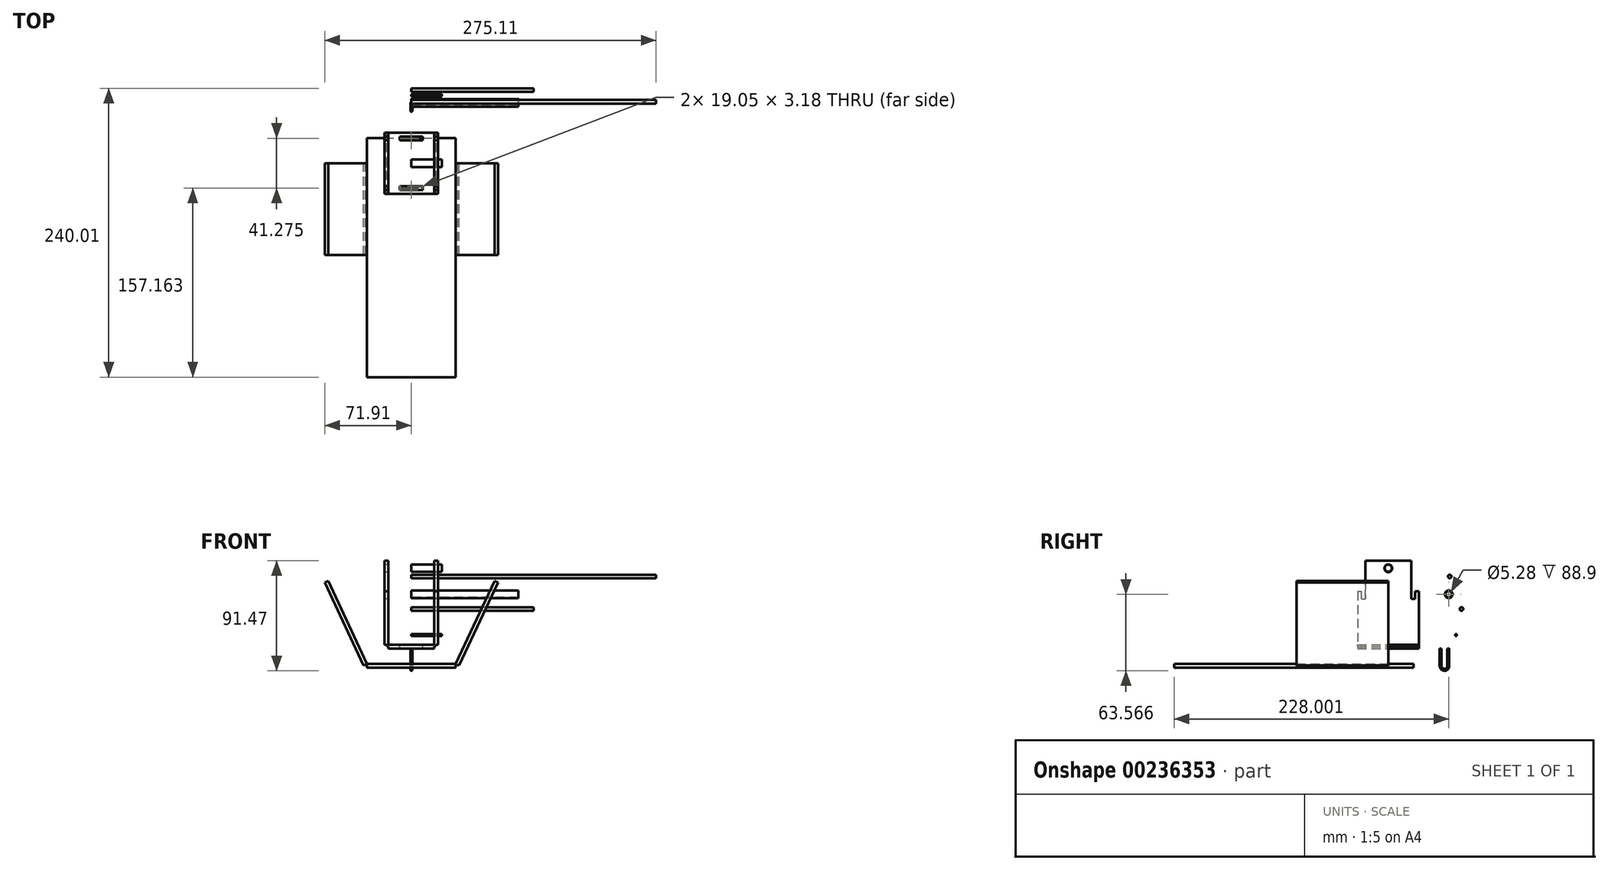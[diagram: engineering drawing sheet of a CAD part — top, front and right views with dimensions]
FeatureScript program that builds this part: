
annotation { "Feature Type Name" : "Feature", "Feature Type Description" : "" }
export const myFeature = defineFeature(function(context is Context, id is Id, definition is map)
    precondition{}
    {
        {
            var Q0;
            Q0=qCreatedBy(makeId("Front.planeOp"),FACE);
            var sketch = newSketch(context, id + "F0", { "sketchPlane" : qUnion([Q0])});
            skLineSegment(sketch, "E0.bottom", {"start": v(-22.22, 47.63) * mm, "end": v(-19.05, 47.63) * mm});
            skLineSegment(sketch, "E0.top", {"start": v(-22.23, 3.18) * mm, "end": v(-20.64, 3.18) * mm});
            skLineSegment(sketch, "E0.left", {"start": v(-22.22, 47.63) * mm, "end": v(-22.23, 3.18) * mm});
            skLineSegment(sketch, "E0.right", {"start": v(-19.05, 47.63) * mm, "end": v(-19.05, 3.18) * mm});
            skLineSegment(sketch, "E1.bottom", {"start": v(-19.05, 3.18) * mm, "end": v(0, 3.18) * mm});
            skLineSegment(sketch, "E1.top", {"start": v(-19.05, 0) * mm, "end": v(0, 0) * mm});
            skLineSegment(sketch, "E1.left", {"start": v(-19.05, 1.59) * mm, "end": v(-19.05, 0) * mm});
            skLineSegment(sketch, "E1.right", {"start": v(0, 3.17) * mm, "end": v(0, 0) * mm});
            skLineSegment(sketch, "E2.MirrorCS", {"start": v(22.23, 47.63) * mm, "end": v(22.23, 3.18) * mm});
            skLineSegment(sketch, "E3.MirrorCS", {"start": v(19.05, 47.63) * mm, "end": v(19.05, 3.17) * mm});
            skLineSegment(sketch, "E4.MirrorCS", {"start": v(22.22, 47.63) * mm, "end": v(19.05, 47.63) * mm});
            skLineSegment(sketch, "E5.MirrorCS", {"start": v(22.23, 3.17) * mm, "end": v(20.64, 3.17) * mm});
            skLineSegment(sketch, "E6.MirrorCS", {"start": v(19.05, 1.59) * mm, "end": v(19.05, 0) * mm});
            skLineSegment(sketch, "E7.MirrorCS", {"start": v(19.05, 3.17) * mm, "end": v(0, 3.17) * mm});
            skLineSegment(sketch, "E8.MirrorCS", {"start": v(19.05, 0) * mm, "end": v(0, 0) * mm});
            skArc(sketch, "E9", {"start": v(-20.64, 3.18) * mm, "mid": v(-20.08, 2.14) * mm, "end": v(-19.05, 1.59) * mm});
            skArc(sketch, "E10", {"start": v(19.05, 1.59) * mm, "mid": v(20.08, 2.14) * mm, "end": v(20.64, 3.18) * mm});
            skPoint(sketch, "E11.orphan", {"position": v(19.05, 3.17) * mm});
            skSolve(sketch);
        }
        {
            var Q0;
            Q0 = qSketchRegion(id + "F0", true);
            extrude(context, id + "F1", {"entities" : qUnion([Q0]), "endBound" : BoundingType.SYMMETRIC, "depth" : 50.8 * mm});
        }
        {
            var Q0;
            Q0=makeQuery(id+"F1.opExtrude","SWEPT_FACE",FACE,{"disambiguationData":[OSD([sQuery(id+"F0.wireOp",EDGE,"E0.left")])]});
            var sketch = newSketch(context, id + "F2", { "sketchPlane" : qUnion([Q0])});
            skLineSegment(sketch, "E12.bottom", {"start": v(19.05, 47.62) * mm, "end": v(22.23, 47.62) * mm});
            skLineSegment(sketch, "E12.top", {"start": v(19.05, 41.27) * mm, "end": v(22.23, 41.27) * mm});
            skLineSegment(sketch, "E12.left", {"start": v(19.05, 47.62) * mm, "end": v(19.05, 41.27) * mm});
            skLineSegment(sketch, "E12.right", {"start": v(22.23, 47.62) * mm, "end": v(22.23, 41.27) * mm});
            skLineSegment(sketch, "E13.MirrorCS", {"start": v(-19.05, 47.62) * mm, "end": v(-19.05, 41.27) * mm});
            skLineSegment(sketch, "E14.MirrorCS", {"start": v(-19.05, 41.27) * mm, "end": v(-22.23, 41.27) * mm});
            skLineSegment(sketch, "E15.MirrorCS", {"start": v(-22.23, 47.62) * mm, "end": v(-22.23, 41.27) * mm});
            skLineSegment(sketch, "E16.MirrorCS", {"start": v(-19.05, 47.62) * mm, "end": v(-22.23, 47.62) * mm});
            skSolve(sketch);
        }
        {
            var Q0;
            Q0 = qSketchRegion(id + "F2", true);
            var Q1;
            Q1=makeQuery(id+"F1.opExtrude","SWEPT_FACE",FACE,{"disambiguationData":[OSD([sQuery(id+"F0.wireOp",EDGE,"E2.MirrorCS")])]});
            extrude(context, id + "F3", {"entities" : qUnion([Q0]), "operationType" : NewBodyOperationType.REMOVE, "endBound" : BoundingType.UP_TO_SURFACE, "oppositeDirection" : true, "endBoundEntityFace" : qUnion([Q1]), "depth" : 25.4 * mm});
        }
        {
            var Q0;
            Q0=makeQuery(id+"F1.opExtrude","SWEPT_FACE",FACE,{"disambiguationData":[OSD([sQuery(id+"F0.wireOp",EDGE,"E1.bottom"),sQuery(id+"F0.wireOp",EDGE,"E7.MirrorCS")])]});
            var sketch = newSketch(context, id + "F4", { "sketchPlane" : qUnion([Q0])});
            skLineSegment(sketch, "E17.bottom", {"start": v(9.52, 22.22) * mm, "end": v(-9.52, 22.22) * mm});
            skLineSegment(sketch, "E17.top", {"start": v(9.52, 19.05) * mm, "end": v(-9.52, 19.05) * mm});
            skLineSegment(sketch, "E17.left", {"start": v(9.52, 22.22) * mm, "end": v(9.52, 19.05) * mm});
            skLineSegment(sketch, "E17.right", {"start": v(-9.53, 22.22) * mm, "end": v(-9.53, 19.05) * mm});
            skPoint(sketch, "E17.middle", {"position": v(0, 20.64) * mm});
            skLineSegment(sketch, "E18.MirrorCS", {"start": v(9.52, -19.05) * mm, "end": v(-9.52, -19.05) * mm});
            skLineSegment(sketch, "E19.MirrorCS", {"start": v(-9.52, -22.22) * mm, "end": v(-9.52, -19.05) * mm});
            skLineSegment(sketch, "E20.MirrorCS", {"start": v(9.52, -22.22) * mm, "end": v(-9.52, -22.22) * mm});
            skLineSegment(sketch, "E21.MirrorCS", {"start": v(9.52, -22.22) * mm, "end": v(9.52, -19.05) * mm});
            skSolve(sketch);
        }
        {
            var Q0;
            Q0 = qSketchRegion(id + "F4", true);
            extrude(context, id + "F5", {"entities" : qUnion([Q0]), "operationType" : NewBodyOperationType.REMOVE, "endBound" : BoundingType.THROUGH_ALL, "oppositeDirection" : true, "depth" : 25.4 * mm});
        }
        {
            var Q0;
            Q0=qCreatedBy(makeId("Front.planeOp"),FACE);
            var sketch = newSketch(context, id + "F6", { "sketchPlane" : qUnion([Q0])});
            skLineSegment(sketch, "E22.bottom", {"start": v(0, -12.7) * mm, "end": v(-36.83, -12.7) * mm});
            skLineSegment(sketch, "E22.top", {"start": v(0, -15.88) * mm, "end": v(-36.83, -15.88) * mm});
            skLineSegment(sketch, "E22.right", {"start": v(-36.83, -14.29) * mm, "end": v(-36.83, -15.88) * mm});
            skLineSegment(sketch, "E23", {"start": v(-36.83, -12.7) * mm, "end": v(-69.03, 56.36) * mm});
            skLineSegment(sketch, "E24", {"start": v(-69.03, 56.36) * mm, "end": v(-71.91, 55.02) * mm});
            skLineSegment(sketch, "E25", {"start": v(-71.91, 55.02) * mm, "end": v(-39.7, -14.04) * mm});
            skLineSegment(sketch, "E26", {"start": v(-39.7, -14.04) * mm, "end": v(-38.27, -13.37) * mm});
            skArc(sketch, "E27", {"start": v(-38.27, -13.37) * mm, "mid": v(-37.65, -13.99) * mm, "end": v(-36.83, -14.29) * mm});
            skLineSegment(sketch, "E28.MirrorCS", {"start": v(0, -12.7) * mm, "end": v(36.83, -12.7) * mm});
            skLineSegment(sketch, "E29.MirrorCS", {"start": v(0, -15.88) * mm, "end": v(36.83, -15.87) * mm});
            skLineSegment(sketch, "E30.MirrorCS", {"start": v(36.83, -12.7) * mm, "end": v(69.03, 56.36) * mm});
            skLineSegment(sketch, "E31.MirrorCS", {"start": v(71.91, 55.02) * mm, "end": v(39.7, -14.04) * mm});
            skLineSegment(sketch, "E32.MirrorCS", {"start": v(39.7, -14.04) * mm, "end": v(38.27, -13.37) * mm});
            skArc(sketch, "E33.MirrorCS", {"start": v(38.27, -13.37) * mm, "mid": v(37.65, -13.99) * mm, "end": v(36.83, -14.29) * mm});
            skLineSegment(sketch, "E34.MirrorCS", {"start": v(69.03, 56.36) * mm, "end": v(71.91, 55.02) * mm});
            skPoint(sketch, "E35.MirrorCS.end.orphan", {"position": v(36.83, -15.88) * mm});
            skPoint(sketch, "E35.MirrorCS.start.orphan", {"position": v(36.83, -14.29) * mm});
            skLineSegment(sketch, "E36", {"start": v(36.83, -14.29) * mm, "end": v(36.83, -15.88) * mm});
            skSolve(sketch);
        }
        {
            var Q0;
            Q0 = qSketchRegion(id + "F6", true);
            extrude(context, id + "F7", {"entities" : qUnion([Q0]), "depth" : 76.2 * mm});
        }
        {
            var Q0;
            Q0=makeQuery(id+"F1.opExtrude","SWEPT_FACE",FACE,{"disambiguationData":[OSD([sQuery(id+"F0.wireOp",EDGE,"E2.MirrorCS")])]});
            var sketch = newSketch(context, id + "F8", { "sketchPlane" : qUnion([Q0])});
            skLineSegment(sketch, "E37.bottom", {"start": v(-19.05, 47.62) * mm, "end": v(19.05, 47.62) * mm});
            skLineSegment(sketch, "E37.top", {"start": v(-19.05, 73.02) * mm, "end": v(19.05, 73.02) * mm});
            skLineSegment(sketch, "E37.left", {"start": v(-19.05, 47.62) * mm, "end": v(-19.05, 73.02) * mm});
            skLineSegment(sketch, "E37.right", {"start": v(19.05, 47.62) * mm, "end": v(19.05, 73.02) * mm});
            skCircle(sketch, "E38", {"center": v(0, 66.68) * mm, "radius": 3.18 * mm});
            skSolve(sketch);
        }
        {
            var Q0;
            Q0 = qSketchRegion(id + "F8", true);
            var Q1;
            Q1=makeQuery(id+"F1.opExtrude","SWEPT_FACE",FACE,{"disambiguationData":[OSD([sQuery(id+"F0.wireOp",EDGE,"E3.MirrorCS")])]});
            extrude(context, id + "F9", {"entities" : qUnion([Q0]), "operationType" : NewBodyOperationType.ADD, "endBound" : BoundingType.UP_TO_SURFACE, "oppositeDirection" : true, "endBoundEntityFace" : qUnion([Q1]), "depth" : 25.4 * mm});
        }
        {
            var Q0;
            Q0=makeQuery(id+"F1.opExtrude","SWEPT_FACE",FACE,{"disambiguationData":[OSD([sQuery(id+"F0.wireOp",EDGE,"E0.left")])]});
            var sketch = newSketch(context, id + "F10", { "sketchPlane" : qUnion([Q0])});
            skLineSegment(sketch, "E39.bottom", {"start": v(-19.05, 47.62) * mm, "end": v(19.05, 47.62) * mm});
            skLineSegment(sketch, "E39.top", {"start": v(-19.05, 73.03) * mm, "end": v(19.05, 73.03) * mm});
            skLineSegment(sketch, "E39.left", {"start": v(-19.05, 47.62) * mm, "end": v(-19.05, 73.03) * mm});
            skLineSegment(sketch, "E39.right", {"start": v(19.05, 47.62) * mm, "end": v(19.05, 73.03) * mm});
            skCircle(sketch, "E40", {"center": v(0, 66.67) * mm, "radius": 3.18 * mm});
            skSolve(sketch);
        }
        {
            var Q0;
            Q0 = qSketchRegion(id + "F10", true);
            var Q1;
            Q1=makeQuery(id+"F1.opExtrude","SWEPT_FACE",FACE,{"disambiguationData":[OSD([sQuery(id+"F0.wireOp",EDGE,"E0.right")])]});
            extrude(context, id + "F11", {"entities" : qUnion([Q0]), "operationType" : NewBodyOperationType.ADD, "endBound" : BoundingType.UP_TO_SURFACE, "oppositeDirection" : true, "endBoundEntityFace" : qUnion([Q1]), "depth" : 25.4 * mm});
        }
        {
            var Q0;
            Q0=makeQuery(id+"F7.opExtrude","SWEPT_FACE",FACE,{"disambiguationData":[OSD([sQuery(id+"F6.wireOp",EDGE,"E22.bottom"),sQuery(id+"F6.wireOp",EDGE,"E28.MirrorCS")])]});
            var sketch = newSketch(context, id + "F12", { "sketchPlane" : qUnion([Q0])});
            skLineSegment(sketch, "E41.bottom", {"start": v(-36.83, 20.96) * mm, "end": v(36.83, 20.96) * mm});
            skLineSegment(sketch, "E41.top", {"start": v(-36.83, -177.8) * mm, "end": v(36.83, -177.8) * mm});
            skLineSegment(sketch, "E41.left", {"start": v(-36.83, 20.96) * mm, "end": v(-36.83, -177.8) * mm});
            skLineSegment(sketch, "E41.right", {"start": v(36.83, 20.96) * mm, "end": v(36.83, -177.8) * mm});
            skSolve(sketch);
        }
        {
            var Q0;
            Q0 = qSketchRegion(id + "F12", true);
            extrude(context, id + "F13", {"entities" : qUnion([Q0]), "operationType" : NewBodyOperationType.ADD, "oppositeDirection" : true, "depth" : 3.17 * mm});
        }
        {
            var Q0;
            Q0=qCreatedBy(makeId("Right.planeOp"),FACE);
            var sketch = newSketch(context, id + "F14", { "sketchPlane" : qUnion([Q0])});
            skCircle(sketch, "E42", {"center": v(0, 66.83) * mm, "radius": 3.15 * mm});
            skCircle(sketch, "E43", {"center": v(0, 66.83) * mm, "radius": 2.9 * mm});
            skSolve(sketch);
        }
        {
            var Q0;
            Q0 = qSketchRegion(id + "F14", true);
            extrude(context, id + "F15", {"entities" : qUnion([Q0]), "depth" : 25.4 * mm});
        }
        {
            var Q0;
            Q0=qCreatedBy(makeId("Right.planeOp"),FACE);
            var sketch = newSketch(context, id + "F16", { "sketchPlane" : qUnion([Q0])});
            skCircle(sketch, "E44", {"center": v(50.2, 45.13) * mm, "radius": 3.18 * mm});
            skCircle(sketch, "E45", {"center": v(50.2, 45.13) * mm, "radius": 2.64 * mm});
            skSolve(sketch);
        }
        {
            var Q0;
            Q0 = qSketchRegion(id + "F16", true);
            extrude(context, id + "F17", {"entities" : qUnion([Q0]), "depth" : 88.9 * mm});
        }
        {
            var Q0;
            Q0=qCreatedBy(makeId("Right.planeOp"),FACE);
            var sketch = newSketch(context, id + "F18", { "sketchPlane" : qUnion([Q0])});
            skCircle(sketch, "E46", {"center": v(51.01, 59.93) * mm, "radius": 1.43 * mm});
            skSolve(sketch);
        }
        {
            var Q0;
            Q0=makeQuery(id+"F18.imprint","IMPRINT",FACE,{"disambiguationData":[TD([[makeQuery(id+"F18.imprint","IMPRINT",EDGE,{"derivedFrom":sQuery(id+"F18.wireOp",EDGE,"E46")}),1.0]])]});
            extrude(context, id + "F19", {"entities" : qUnion([Q0]), "depth" : 203.2 * mm});
        }
        {
            var Q0;
            Q0=qCreatedBy(makeId("Right.planeOp"),FACE);
            var sketch = newSketch(context, id + "F20", { "sketchPlane" : qUnion([Q0])});
            skCircle(sketch, "E47", {"center": v(60.75, 32.96) * mm, "radius": 1.46 * mm});
            skSolve(sketch);
        }
        {
            var Q0;
            Q0 = qSketchRegion(id + "F20", true);
            extrude(context, id + "F21", {"entities" : qUnion([Q0]), "depth" : 101.6 * mm});
        }
        {
            var Q0;
            Q0=qCreatedBy(makeId("Right.planeOp"),FACE);
            var sketch = newSketch(context, id + "F22", { "sketchPlane" : qUnion([Q0])});
            skArc(sketch, "E48", {"start": v(43.5, -14.5) * mm, "mid": v(46.67, -17.68) * mm, "end": v(49.85, -14.5) * mm});
            skLineSegment(sketch, "E49", {"start": v(49.85, -14.5) * mm, "end": v(49.85, 0) * mm});
            skLineSegment(sketch, "E50", {"start": v(43.5, -14.5) * mm, "end": v(43.5, 0) * mm});
            skSolve(sketch);
        }
        {
            var Q0;
            Q0=qCreatedBy(makeId("Top.planeOp"),FACE);
            var sketch = newSketch(context, id + "F23", { "sketchPlane" : qUnion([Q0])});
            skCircle(sketch, "E51", {"center": v(0, 43.5) * mm, "radius": 0.76 * mm});
            skSolve(sketch);
        }
        {
            var Q0;
            Q0 = qSketchRegion(id + "F23", true);
            var Q1;
            Q1 = qConstructionFilter(qBodyType(qCreatedBy(id + "F22" ,EDGE), BodyType.WIRE), ConstructionObject.NO);
            sweep(context, id + "F24", {"profiles" : qUnion([Q0]), "path" : qUnion([Q1])});
        }
        {
            var Q0;
            Q0=qCreatedBy(makeId("Right.planeOp"),FACE);
            var sketch = newSketch(context, id + "F25", { "sketchPlane" : qUnion([Q0])});
            skCircle(sketch, "E52", {"center": v(56.29, 11.26) * mm, "radius": 0.76 * mm});
            skSolve(sketch);
        }
        {
            var Q0;
            Q0 = qSketchRegion(id + "F25", true);
            extrude(context, id + "F26", {"entities" : qUnion([Q0]), "depth" : 25.4 * mm});
        }
    });
